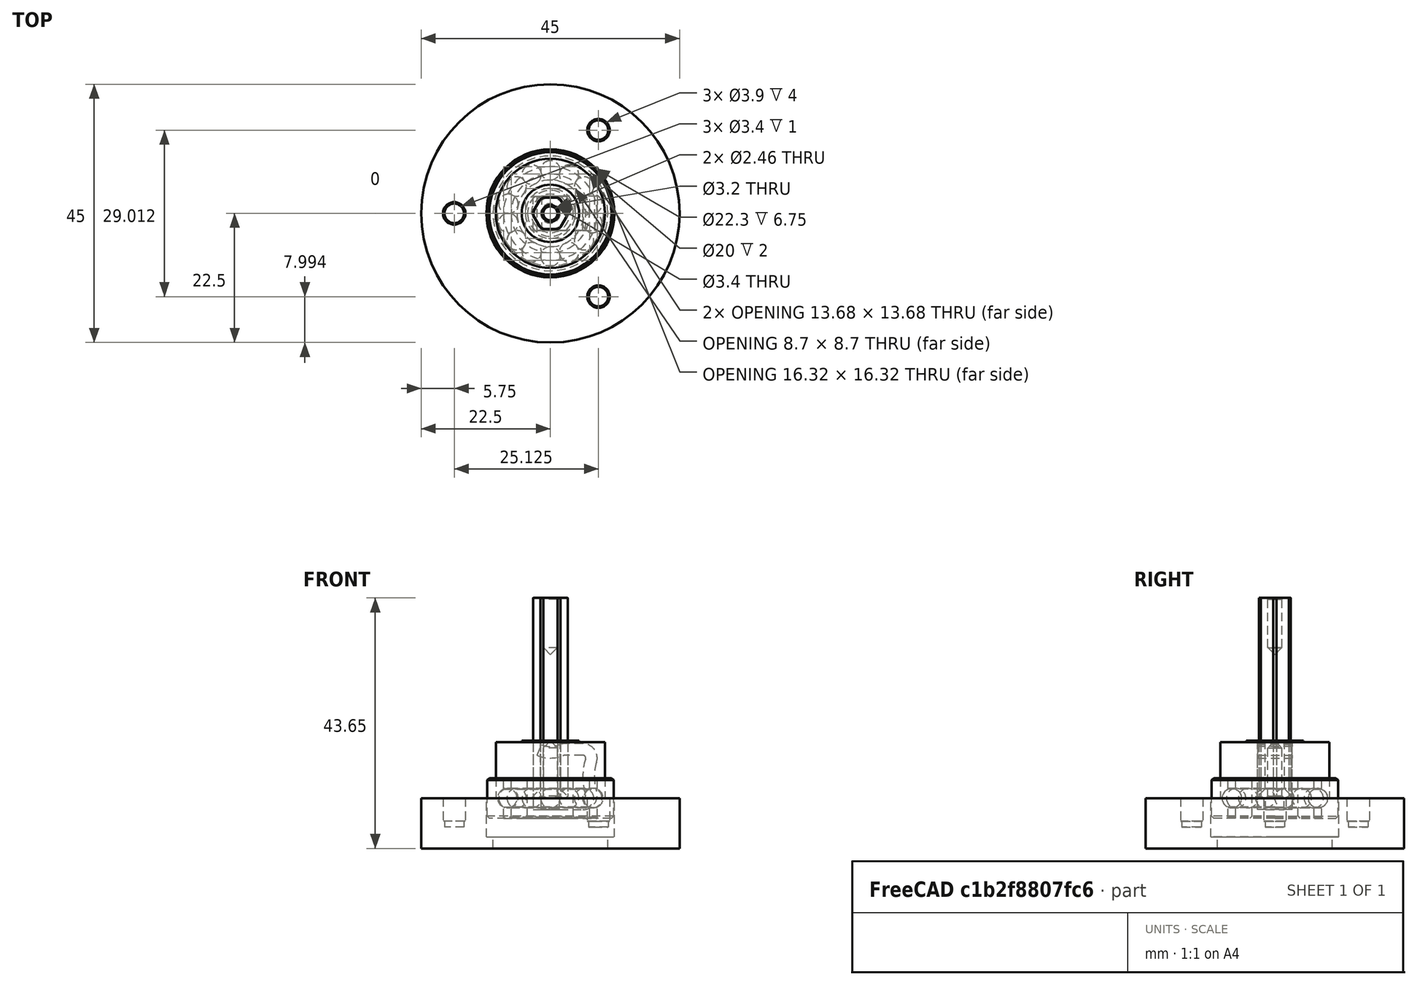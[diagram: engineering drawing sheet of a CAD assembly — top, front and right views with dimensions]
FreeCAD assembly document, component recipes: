
FREECAD ASSEMBLY — COMPONENT RECIPES ("Parts")

This assembly document has 5 components, labeled P0..P4 below (a component is one placed body or linked part). 3 of them carry a construction recipe — the FreeCAD feature program that regenerates the part from scratch, quoted from this document or its linked companion documents; the rest are supplied as boundary geometry only. No exploded tour is included for this assembly.
COMPONENT P0 — recipe-attached ("BearinEndCover", modeled in this document).
Construction recipe (the document's own serialized feature program — sketch geometry with constraints, then the solid features built on it; lengths are millimeters unless a unit is written):

FEATURE [Sketcher::SketchObject] Sketch005
  ArcFitTolerance = 0
  AttachmentSupport = -> [XZ_Plane007]
  FullyConstrained = true
  MakeInternals = false
  MapMode = 5
  Placement = pos=(0,0,0) rot=(1,0,0;1.5708rad)
  expr: Constraints[13] = <<Dimensions>>.bearing_Da / 2 - 2 * <<Dimensions>>.clearance_loose_fit
  expr: Constraints[14] = 10 mm
  expr: Constraints[15] = <<Dimensions>>.bearing_da / 2
  expr: Constraints[16] = <<Dimensions>>.clearance_loose_fit
  sketch-geometry (6):
    g0: LineSegment StartX=0 StartY=0 StartZ=0 EndX=0 EndY=10 EndZ=0
    g1: LineSegment StartX=0 StartY=10 StartZ=0 EndX=5 EndY=10 EndZ=0
    g2: LineSegment StartX=5 StartY=10 StartZ=0 EndX=5 EndY=9.75 EndZ=0
    g3: LineSegment StartX=5 StartY=9.75 StartZ=0 EndX=9.5 EndY=9.75 EndZ=0
    g4: LineSegment StartX=9.5 StartY=9.75 StartZ=0 EndX=9.5 EndY=0 EndZ=0
    g5: LineSegment StartX=9.5 StartY=0 StartZ=0 EndX=0 EndY=0 EndZ=0
  constraints (17):
    c: Coincident(g-1,g0)
    c: Coincident(g0,g1)
    c: Horizontal(g1)
    c: Coincident(g1,g2)
    c: Vertical(g2)
    c: Coincident(g2,g3)
    c: Horizontal(g3)
    c: Coincident(g3,g4)
    c: Vertical(g4)
    c: Coincident(g4,g5)
    c: Coincident(g5,g0)
    c: Horizontal(g5)
    c: Vertical(g0)
    c: DistanceX(g5,g5) = 9.5
    c: DistanceY(g0,g0) = 10
    c: DistanceX(g1,g1) = 5
    c: DistanceY(g2,g2) = 0.25
FEATURE [PartDesign::Revolution] Revolution001
  Angle = 360
  Angle2 = 60
  Axis = (0,2e-16,1)
  Base = (0,0,0)
  Placement = pos=(0,0,0) rot=(1,0,0;1.5708rad)
  Profile = -> Sketch005
  ReferenceAxis = -> Sketch005 [V_Axis]
  Reversed = true
  Suppressed = false
  Type = 0
FEATURE [Sketcher::SketchObject] Sketch006
  ArcFitTolerance = 0
  AttachmentSupport = -> [XY_Plane007]
  FullyConstrained = true
  MakeInternals = false
  MapMode = 5
  expr: Constraints[1] = <<Dimensions>>.shaft_end_cover_screw_diameter
  sketch-geometry (1):
    g0: Circle CenterX=0 CenterY=0 CenterZ=0 NormalX=0 NormalY=0 NormalZ=1 AngleXU=0 Radius=1.5
  constraints (2):
    c: Coincident(g0,g-1)
    c: Diameter(g0) = 3
FEATURE [PartDesign::Hole] Hole002
  BaseFeature = -> Revolution001
  CustomThreadClearance = 0
  Depth = 54.4277
  DepthType = 1
  Diameter = 3.4
  DrillForDepth = false
  DrillPoint = 1
  DrillPointAngle = 118
  HoleCutCountersinkAngle = 90
  HoleCutCustomValues = false
  HoleCutDepth = 0
  HoleCutDiameter = 6.7
  HoleCutType = 5
  ModelThread = false
  Placement = pos=(0,0,0) rot=(1,0,0;1.5708rad)
  Profile = -> Sketch006
  Reversed = true
  Suppressed = false
  Tapered = false
  TaperedAngle = 90
  ThreadClass = 0
  ThreadDepth = 54.4277
  ThreadDepthType = 0
  ThreadDirection = 0
  ThreadFit = 0
  ThreadSize = 9
  ThreadType = 1
  Threaded = false
  UseCustomThreadClearance = false
  expr: ThreadSize = <<Dimensions>>.shaft_end_cover_screw_type
FEATURE [PartDesign::Body] Body002  label="Body"
  AllowCompound = false
  Group = -> [Sketch005,Revolution001,Sketch006,Hole002]
  Origin = -> Origin007
  Tip = -> Hole002
COMPONENT P1 — recipe-attached ("BearingHousing", modeled in this document).
Construction recipe (the document's own serialized feature program — sketch geometry with constraints, then the solid features built on it; lengths are millimeters unless a unit is written):

FEATURE [Sketcher::SketchObject] Sketch003
  ArcFitTolerance = 0
  AttachmentSupport = -> [XZ_Plane005]
  FullyConstrained = true
  MakeInternals = false
  MapMode = 5
  Placement = pos=(0,0,0) rot=(1,0,0;1.5708rad)
  expr: Constraints[12] = <<Dimensions>>.bearing_D / 2 + <<Dimensions>>.clearance_tight_fit
  expr: Constraints[13] = <<Dimensions>>.bearing_housing_min_thickness
  expr: Constraints[14] = <<Dimensions>>.bearing_B - <<Dimensions>>.clearance_loose_fit
  expr: Constraints[15] = <<Dimensions>>.bearing_Da / 2
  expr: Constraints[17] = <<Dimensions>>.bearing_housing_diameter / 2
  sketch-geometry (6):
    g0: LineSegment StartX=-22.5 StartY=0 StartZ=0 EndX=-22.5 EndY=-8.75 EndZ=0
    g1: LineSegment StartX=-22.5 StartY=-8.75 StartZ=0 EndX=-10 EndY=-8.75 EndZ=0
    g2: LineSegment StartX=-10 StartY=-8.75 StartZ=0 EndX=-10 EndY=-6.75 EndZ=0
    g3: LineSegment StartX=-10 StartY=-6.75 StartZ=0 EndX=-11.15 EndY=-6.75 EndZ=0
    g4: LineSegment StartX=-11.15 StartY=-6.75 StartZ=0 EndX=-11.15 EndY=0 EndZ=0
    g5: LineSegment StartX=-22.5 StartY=0 StartZ=0 EndX=-11.15 EndY=0 EndZ=0
  constraints (18):
    c: PointOnObject(g0,g-1)
    c: Vertical(g0)
    c: Horizontal(g1)
    c: Coincident(g2,g1)
    c: Vertical(g2)
    c: Coincident(g3,g2)
    c: Horizontal(g3)
    c: Coincident(g4,g3)
    c: PointOnObject(g4,g-1)
    c: Vertical(g4)
    c: Coincident(g5,g0)
    c: Coincident(g5,g4)
    c: DistanceX(g4,g-1) = 11.15
    c: DistanceY(g2,g2) = 2
    c: DistanceY(g4,g4) = 6.75
    c: DistanceX(g1,g-1) = 10
    c: Coincident(g1,g0)
    c: DistanceX(g0,g-1) = 22.5
FEATURE [PartDesign::Revolution] Revolution
  Angle = 360
  Angle2 = 60
  Axis = (0,2e-16,1)
  Base = (0,0,0)
  Placement = pos=(0,0,0) rot=(1,0,0;1.5708rad)
  Profile = -> Sketch003
  ReferenceAxis = -> Sketch003 [V_Axis]
  Suppressed = false
  Type = 0
FEATURE [Sketcher::SketchObject] Sketch004
  ArcFitTolerance = 0
  AttachmentSupport = -> [XY_Plane005]
  FullyConstrained = true
  MakeInternals = false
  MapMode = 5
  expr: Constraints[1] = <<Dimensions>>.bearing_D / 4 + <<Dimensions>>.bearing_housing_diameter / 4
  expr: Constraints[2] = <<Dimensions>>.bearing_housing_screw_diameter
  sketch-geometry (1):
    g0: Circle CenterX=-16.75 CenterY=0 CenterZ=0 NormalX=0 NormalY=0 NormalZ=1 AngleXU=0 Radius=1.5
  constraints (3):
    c: PointOnObject(g0,g-1)
    c: Distance(g0,g-1) = 16.75
    c: Diameter(g0) = 3
FEATURE [PartDesign::Hole] Hole001  label="Hole_Attachment"
  BaseFeature = -> Revolution
  CustomThreadClearance = 0
  Depth = 5
  DepthType = 0
  Diameter = 3.4
  DrillForDepth = false
  DrillPoint = 0
  DrillPointAngle = 118
  HoleCutCountersinkAngle = 90
  HoleCutCustomValues = false
  HoleCutDepth = 4
  HoleCutDiameter = 3.9
  HoleCutType = 1
  ModelThread = false
  Placement = pos=(0,0,0) rot=(1,0,0;1.5708rad)
  Profile = -> Sketch004
  Suppressed = false
  Tapered = false
  TaperedAngle = 90
  ThreadClass = 0
  ThreadDepth = 5
  ThreadDepthType = 0
  ThreadDirection = 0
  ThreadFit = 0
  ThreadSize = 9
  ThreadType = 1
  Threaded = false
  UseCustomThreadClearance = false
  expr: Depth = <<Dimensions>>.bearing_housing_screw_length + <<Dimensions>>.screw_hole_extra_depth - <<Dimensions>>.frame_thickness
  expr: HoleCutDepth = <<Dimensions>>.bearing_housing_ti_L
  expr: HoleCutDiameter = <<Dimensions>>.bearing_housing_ti_D
  expr: ThreadSize = <<Dimensions>>.bearing_housing_screw_type
FEATURE [PartDesign::PolarPattern] PolarPattern
  Angle = 360
  Axis = -> Z_Axis005
  BaseFeature = -> Hole001
  Mode = 0
  Occurrences = 3
  Offset = 120
  Originals = -> [Hole001]
  Placement = pos=(0,0,0) rot=(1,0,0;1.5708rad)
  Suppressed = false
  TransformMode = 0
FEATURE [PartDesign::Body] Body001  label="BearingHousingBody"
  AllowCompound = false
  Group = -> [Sketch003,Revolution,Sketch004,Hole001,PolarPattern]
  Origin = -> Origin005
  Tip = -> PolarPattern
COMPONENT P2 — recipe-attached ("MirrorClip", modeled in this document).
Construction recipe (the document's own serialized feature program — sketch geometry with constraints, then the solid features built on it; lengths are millimeters unless a unit is written):

FEATURE [Sketcher::SketchObject] Sketch
  ArcFitTolerance = 0
  AttachmentSupport = -> [XZ_Plane003]
  FullyConstrained = true
  MakeInternals = false
  MapMode = 5
  Placement = pos=(0,0,0) rot=(1,0,0;1.5708rad)
  expr: Constraints[10] = <<Dimensions>>.mirror_frame_thickness + 2 * <<Dimensions>>.clearance_loose_fit
  expr: Constraints[13] = <<Dimensions>>.mirror_frame_width + <<Dimensions>>.clearance_tight_fit
  expr: Constraints[19] = 0.5 mm
  expr: Constraints[23] = <<Dimensions>>.mirror_adjustment_screw_diameter / 2 + <<Dimensions>>.mirror_clip_edge_distance
  expr: Constraints[5] = <<Dimensions>>.mirror_clip_width / 2
  expr: Constraints[6] = <<Dimensions>>.mirror_clip_minimum_bend_radius
  sketch-geometry (9):
    g0: LineSegment StartX=-3 StartY=0 StartZ=0 EndX=5.65 EndY=0 EndZ=0
    g1: LineSegment StartX=5.65 StartY=7.5 StartZ=0 EndX=2.5 EndY=7.5 EndZ=0
    g2: ArcOfCircle CenterX=0 CenterY=13 CenterZ=0 NormalX=0 NormalY=0 NormalZ=1 AngleXU=0 Radius=6 StartAngle=4.3176 EndAngle=5.10718
    g3: ArcOfCircle CenterX=5.65 CenterY=7 CenterZ=0 NormalX=0 NormalY=0 NormalZ=1 AngleXU=0 Radius=0.5 StartAngle=5.97789 EndAngle=7.85398
    g4: ArcOfCircle CenterX=5.65 CenterY=0.5 CenterZ=0 NormalX=0 NormalY=0 NormalZ=1 AngleXU=0 Radius=0.5 StartAngle=4.71239 EndAngle=6.58848
    g5: GeomPoint [constr] X=0 Y=7 Z=0
    g6: ArcOfCircle CenterX=15.9625 CenterY=3.75 CenterZ=0 NormalX=0 NormalY=0 NormalZ=1 AngleXU=0 Radius=10.3125 StartAngle=2.83629 EndAngle=3.44689
    g7: GeomPoint [constr] X=5.65 Y=3.75 Z=0
    g8: ArcOfCircle CenterX=2.5 CenterY=7 CenterZ=0 NormalX=0 NormalY=0 NormalZ=1 AngleXU=0 Radius=0.5 StartAngle=1.5708 EndAngle=1.96559
  constraints (25):
    c: Horizontal(g0)
    c: Horizontal(g1)
    c: Tangent(g1,g3) = -1.5708
    c: Tangent(g0,g4) = -1.5708
    c: PointOnObject(g0,g-1)
    c: DistanceX(g0,g-1) = 3
    c: Radius(g4) = 0.5
    c: Equal(g3,g4)
    c: PointOnObject(g5,g2)
    c: Vertical(g5,g2)
    c: DistanceY(g0,g1) = 7.5
    c: PointOnObject(g5,g-2)
    c: PointOnObject(g7,g6)
    c: DistanceX(g1,g1) = 3.15
    c: Tangent(g6,g3) = 1.5708
    c: Tangent(g6,g4) = 1.5708
    c: Vertical(g1,g7)
    c: Vertical(g7,g0)
    c: Horizontal(g7,g6)
    c: DistanceY(g5,g1) = 0.5
    c: Horizontal(g2,g2)
    c: Tangent(g8,g1) = -1.5708
    c: Tangent(g8,g2) = 1.5708
    c: DistanceX(g5,g1) = 2.5
    c: Equal(g8,g3)
FEATURE [PartDesign::Plane] DatumPlane  label="Plane_Bottom"
  AttachmentOffset = pos=(0,0,-2) rot=(0,0,1;0rad)
  AttachmentSupport = -> [XY_Plane003]
  Length = 60
  MapMode = 5
  Placement = pos=(0,0,-2) rot=(0,0,1;0rad)
  ResizeMode = 0
  Width = 60
  expr: .AttachmentOffset.Base.z = -<<Dimensions>>.mirror_clip_thickness
FEATURE [Sketcher::SketchObject] Sketch002
  ArcFitTolerance = 0
  AttachmentSupport = -> [DatumPlane]
  FullyConstrained = true
  MakeInternals = false
  MapMode = 5
  Placement = pos=(0,0,-2) rot=(0,0,1;0rad)
  expr: Constraints[1] = <<Dimensions>>.mirror_adjustment_screw_diameter
  sketch-geometry (1):
    g0: Circle CenterX=0 CenterY=0 CenterZ=0 NormalX=0 NormalY=0 NormalZ=1 AngleXU=0 Radius=1.5
  constraints (2):
    c: Coincident(g0,g-1)
    c: Diameter(g0) = 3
FEATURE [PartDesign::Plane] DatumPlane001  label="Plane_Top"
  AttachmentSupport = -> [XY_Plane003]
  Length = 60
  MapMode = 5
  ResizeMode = 0
  Width = 60
FEATURE [Sketcher::SketchObject] Sketch001  label="Profile"
  ArcFitTolerance = 0
  AttachmentSupport = -> [YZ_Plane003]
  ExternalGeometry = -> [DatumPlane,DatumPlane001]
  FullyConstrained = true
  MakeInternals = false
  MapMode = 5
  Placement = pos=(0,0,0) rot=(0.57735,0.57735,0.57735;2.0944rad)
  expr: Constraints[7] = <<Dimensions>>.mirror_clip_width
  sketch-geometry (4):
    g0: LineSegment StartX=-3 StartY=9e-16 StartZ=0 EndX=3 EndY=9e-16 EndZ=0
    g1: LineSegment StartX=3 StartY=9e-16 StartZ=0 EndX=3 EndY=-2 EndZ=0
    g2: LineSegment StartX=3 StartY=-2 StartZ=0 EndX=-3 EndY=-2 EndZ=0
    g3: LineSegment StartX=-3 StartY=-2 StartZ=0 EndX=-3 EndY=9e-16 EndZ=0
  constraints (11):
    c: Coincident(g0,g1)
    c: Coincident(g1,g2)
    c: Coincident(g2,g3)
    c: Coincident(g3,g0)
    c: Horizontal(g0)
    c: Vertical(g1)
    c: Vertical(g3)
    c: DistanceX(g0,g0) = 6
    c: PointOnObject(g0,g-4)
    c: Symmetric(g2,g1,g-2)
    c: PointOnObject(g1,g-3)
FEATURE [PartDesign::AdditivePipe] AdditivePipe
  AuxilleryCurvelinear = true
  AuxillerySpineTangent = false
  Binormal = (0,0,0)
  Mode = 0
  Placement = pos=(0,0,0) rot=(1,1,1;2.0944rad)
  Profile = -> Sketch001
  Refine = true
  Spine = -> Sketch
  SpineTangent = false
  Suppressed = false
  Transformation = 0
  Transition = 0
FEATURE [PartDesign::Hole] Hole
  BaseFeature = -> AdditivePipe
  CustomThreadClearance = 0
  Depth = 2
  DepthType = 0
  Diameter = 3.2
  DrillForDepth = false
  DrillPoint = 1
  DrillPointAngle = 118
  HoleCutCountersinkAngle = 90
  HoleCutCustomValues = false
  HoleCutDepth = 0
  HoleCutDiameter = 6.1
  HoleCutType = 0
  ModelThread = false
  Placement = pos=(0,0,0) rot=(1,1,1;2.0944rad)
  Profile = -> Sketch002
  Reversed = true
  Suppressed = false
  Tapered = false
  TaperedAngle = 90
  ThreadClass = 0
  ThreadDepth = 2
  ThreadDepthType = 0
  ThreadDirection = 0
  ThreadFit = 1
  ThreadSize = 9
  ThreadType = 1
  Threaded = false
  UseCustomThreadClearance = false
  expr: Depth = <<Dimensions>>.mirror_clip_thickness
  expr: ThreadSize = <<Dimensions>>.mirror_adjustment_screw_type
FEATURE [PartDesign::Body] Body  label="MirrorClipBody"
  AllowCompound = false
  Group = -> [DatumPlane001,DatumPlane,Sketch,Sketch001,AdditivePipe,Sketch002,Hole]
  Origin = -> Origin003
  Tip = -> Hole
COMPONENT P3 — geometry summary ("Standoff"; no construction recipe available for this part):
  bounding box: 34.9 x 6.0 x 5.5 mm
  tessellated surface: 4,380 triangles
  volume: 817 mm^3 (71% of its bounding box)
  symmetry: 2-fold rotationally symmetric about the x axis; 2-fold rotationally symmetric about the y axis; revolution-symmetric about the z axis through its bounding-box center; mirror-symmetric across its z mid-plane
COMPONENT P4 — geometry summary ("Bearing"; no construction recipe available for this part):
  bounding box: 22.0 x 22.0 x 7.0 mm
  tessellated surface: 145,344 triangles
  volume: 2131 mm^3 (63% of its bounding box)
  symmetry: 2-fold rotationally symmetric about the y axis; revolution-symmetric about the z axis through its bounding-box center; mirror-symmetric across its x mid-plane, y mid-plane, z mid-plane
PROVENANCE & LICENSES
A FreeCAD (.FCStd) document from a public repository crawl; recipes are the document's own serialized feature recipes (and, for linked parts, companion documents' recipes).
License: gpl-3.0.
